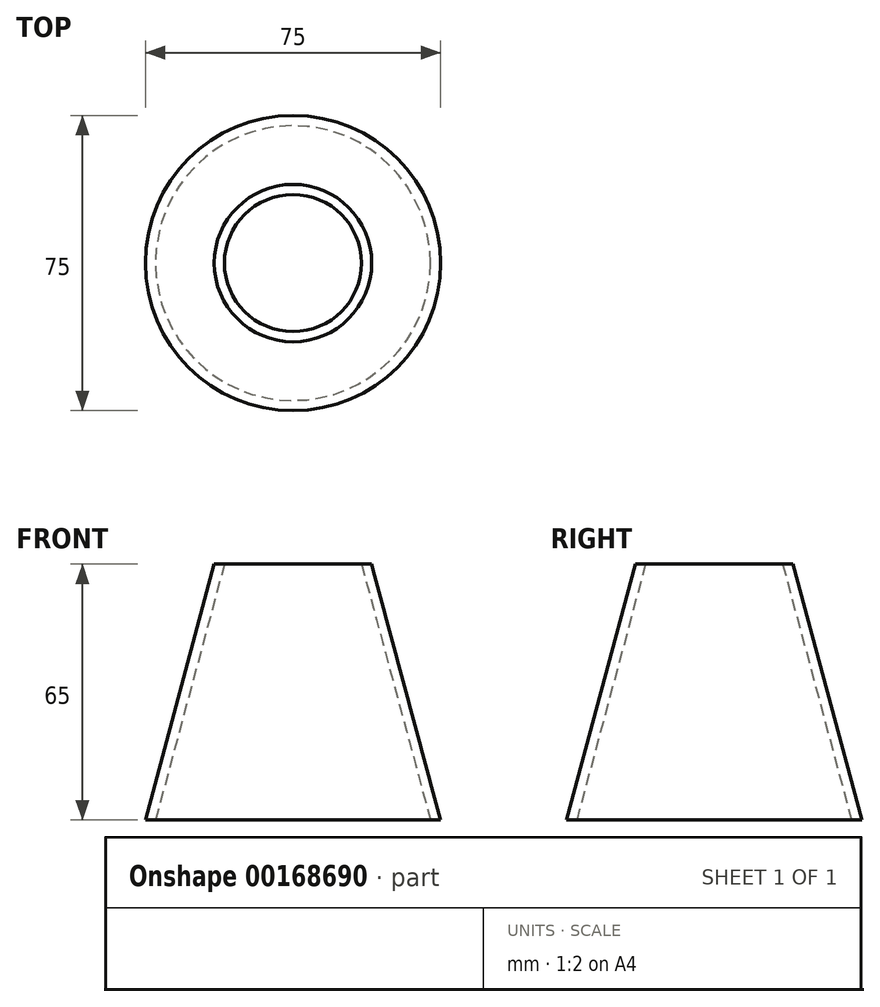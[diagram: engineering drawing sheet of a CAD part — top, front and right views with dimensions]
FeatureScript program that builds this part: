
annotation { "Feature Type Name" : "Feature", "Feature Type Description" : "" }
export const myFeature = defineFeature(function(context is Context, id is Id, definition is map)
    precondition{}
    {
        {
            var Q0;
            Q0=qCreatedBy(makeId("Top.planeOp"),FACE);
            var sketch = newSketch(context, id + "F0", { "sketchPlane" : qUnion([Q0])});
            skLineSegment(sketch, "E0.bottom", {"start": v(-59.09, 42.2) * mm, "end": v(59.09, 42.2) * mm});
            skLineSegment(sketch, "E0.top", {"start": v(-59.09, -42.2) * mm, "end": v(59.09, -42.2) * mm});
            skLineSegment(sketch, "E0.left", {"start": v(-59.09, 42.2) * mm, "end": v(-59.09, -42.2) * mm});
            skLineSegment(sketch, "E0.right", {"start": v(59.09, 42.2) * mm, "end": v(59.09, -42.2) * mm});
            skPoint(sketch, "E0.middle", {"position": v(0, 0) * mm});
            skCircle(sketch, "E1", {"center": v(0, 0) * mm, "radius": 37.5 * mm});
            skSolve(sketch);
        }
        {
            var Q0;
            Q0=qCreatedBy(makeId("Top.planeOp"),FACE);
            cPlane(context, id + "F1", {"entities" : qUnion([Q0]), "cplaneType" : CPlaneType.OFFSET, "offset" : 65 * mm, "width" : 150 * mm, "height" : 150 * mm});
        }
        {
            var Q0;
            Q0=qCreatedBy(id+"F1.planeOp",FACE);
            var sketch = newSketch(context, id + "F2", { "sketchPlane" : qUnion([Q0])});
            skPoint(sketch, "E2.0", {"position": v(0, 0) * mm});
            skCircle(sketch, "E3", {"center": v(0, 0) * mm, "radius": 20 * mm});
            skSolve(sketch);
        }
        {
            var Q0;
            Q0=makeQuery(id+"F0.imprint","IMPRINT",FACE,{"disambiguationData":[TD([[makeQuery(id+"F0.imprint","IMPRINT",EDGE,{"derivedFrom":sQuery(id+"F0.wireOp",EDGE,"E1")}),1.0]])]});
            var Q1;
            Q1=makeQuery(id+"F2.imprint","IMPRINT",FACE,{"disambiguationData":[TD([[makeQuery(id+"F2.imprint","IMPRINT",EDGE,{"derivedFrom":sQuery(id+"F2.wireOp",EDGE,"E3")}),1.0]])]});
            loft(context, id + "F3", {"sheetProfilesArray" : [{ "sheetProfileEntities" : qUnion([Q0]) }, { "sheetProfileEntities" : qUnion([Q1]) }]});
        }
        {
            var Q0;
            Q0=makeQuery(id+"F3.opLoft","CAP_FACE",FACE,{"disambiguationData":[OSD([makeQuery(id+"F2.imprint","IMPRINT",FACE,{"disambiguationData":[TD([[makeQuery(id+"F2.imprint","IMPRINT",EDGE,{"derivedFrom":sQuery(id+"F2.wireOp",EDGE,"E3")}),1.0]])]})])],"isStart":true});
            var Q1;
            Q1=makeQuery(id+"F3.opLoft","CAP_FACE",FACE,{"disambiguationData":[OSD([makeQuery(id+"F0.imprint","IMPRINT",FACE,{"disambiguationData":[TD([[makeQuery(id+"F0.imprint","IMPRINT",EDGE,{"derivedFrom":sQuery(id+"F0.wireOp",EDGE,"E1")}),1.0]])]})])],"isStart":true});
            shell(context, id + "F4", {"entities" : qUnion([Q0, Q1]), "thickness" : 2.5 * mm});
        }
    });
